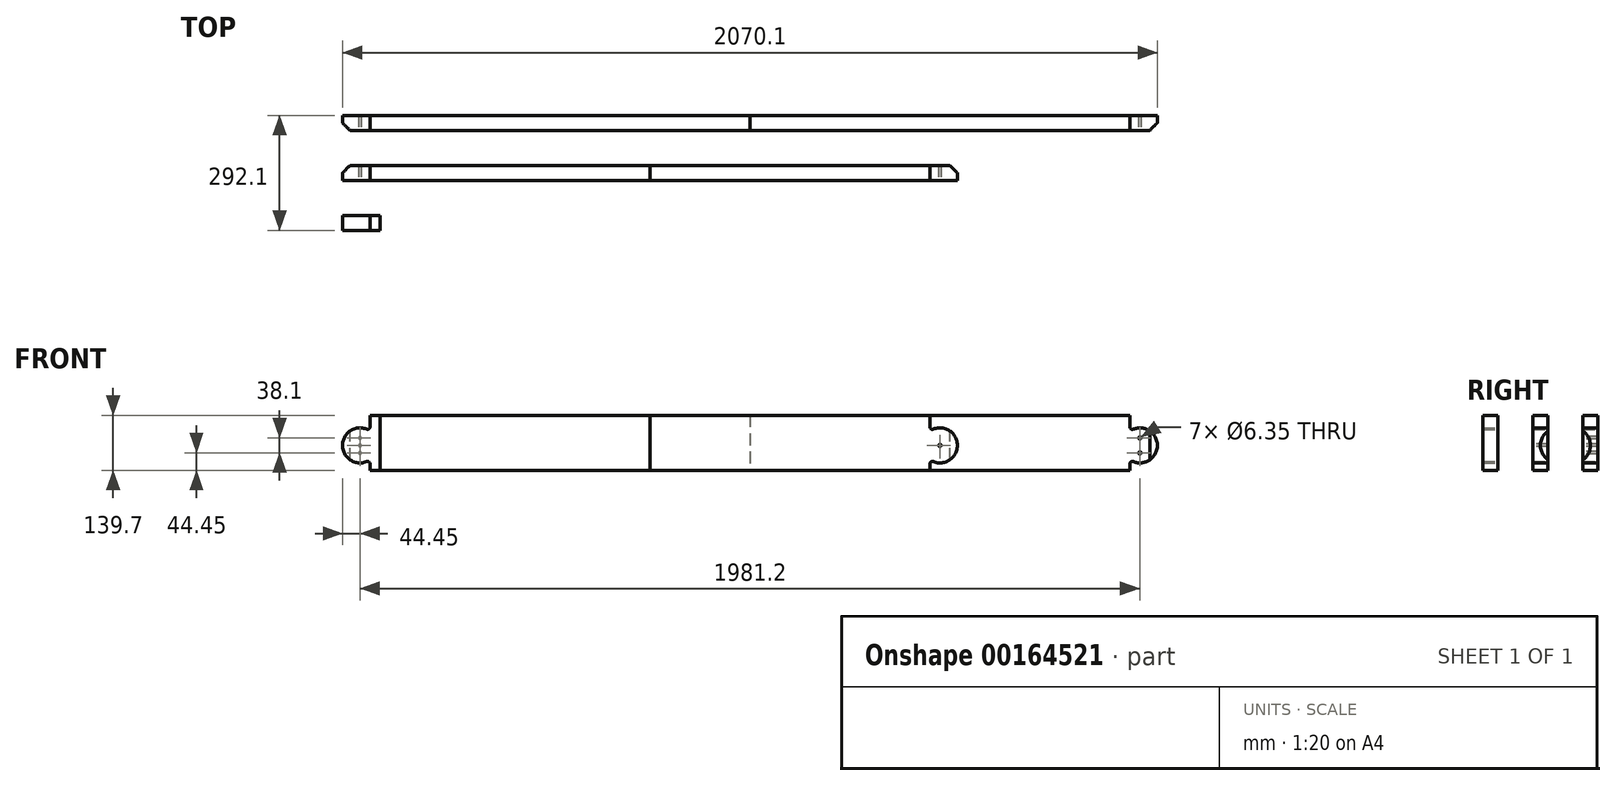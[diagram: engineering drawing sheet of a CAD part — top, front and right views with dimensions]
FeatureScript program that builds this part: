
annotation { "Feature Type Name" : "Feature", "Feature Type Description" : "" }
export const myFeature = defineFeature(function(context is Context, id is Id, definition is map)
    precondition{}
    {
        {
            var Q0;
            Q0=qCreatedBy(makeId("Front.planeOp"),FACE);
            var sketch = newSketch(context, id + "F0", { "sketchPlane" : qUnion([Q0])});
            skArc(sketch, "E0", {"start": v(25.4, 36.48) * mm, "mid": v(-44.45, 0) * mm, "end": v(25.4, -36.48) * mm});
            skLineSegment(sketch, "E1.bottom", {"start": v(50.8, 76.2) * mm, "end": v(25.4, 76.2) * mm});
            skLineSegment(sketch, "E1.top", {"start": v(50.8, -63.5) * mm, "end": v(25.4, -63.5) * mm});
            skLineSegment(sketch, "E1.left", {"start": v(50.8, 76.2) * mm, "end": v(50.8, -63.5) * mm});
            skLineSegment(sketch, "E1.right", {"start": v(25.4, 76.2) * mm, "end": v(25.4, 36.48) * mm});
            skPoint(sketch, "E1.middle", {"position": v(38.1, 6.35) * mm});
            skLineSegment(sketch, "E2.trimOffspring", {"start": v(25.4, -36.48) * mm, "end": v(25.4, -63.5) * mm});
            skSolve(sketch);
        }
        {
            var Q0;
            Q0=makeQuery(id+"F0.imprint","IMPRINT",FACE,{"disambiguationData":[TD([[makeQuery(id+"F0.imprint","IMPRINT",EDGE,{"derivedFrom":sQuery(id+"F0.wireOp",EDGE,"E0")}),1.0]])]});
            extrude(context, id + "F1", {"entities" : qUnion([Q0]), "depth" : 38.1 * mm});
        }
        {
            var Q0;
            Q0=makeQuery(id+"F1.opExtrude","SWEPT_EDGE",EDGE,{"disambiguationData":[OSD([sQuery(id+"F0.wireOp",EDGE,"E0"),sQuery(id+"F0.wireOp",EDGE,"E1.right")])]});
            var Q1;
            Q1=makeQuery(id+"F1.opExtrude","SWEPT_EDGE",EDGE,{"disambiguationData":[OSD([sQuery(id+"F0.wireOp",EDGE,"E0"),sQuery(id+"F0.wireOp",EDGE,"E2.trimOffspring")])]});
            fillet(context, id + "F2", {"entities" : qUnion([Q0, Q1]), "radius" : 6.35 * mm, "tangentPropagation" : true, "allowEdgeOverflow" : false});
        }
        {
            var Q0;
            Q0=makeQuery(id+"F1.opExtrude","SWEPT_BODY",BODY,{"disambiguationData":[OSD([sQuery(id+"F0.wireOp",EDGE,"E0"),sQuery(id+"F0.wireOp",EDGE,"E1.bottom"),sQuery(id+"F0.wireOp",EDGE,"E1.top"),sQuery(id+"F0.wireOp",EDGE,"E1.left"),sQuery(id+"F0.wireOp",EDGE,"E1.right"),sQuery(id+"F0.wireOp",EDGE,"E2.trimOffspring")])]});
            transform(context, id + "F3", {"entities" : qUnion([Q0]), "transformType" : TransformType.TRANSLATION_3D, "dx" : 0 * mm, "dy" : 254 * mm, "dz" : 0 * mm, "makeCopy" : true});
        }
        {
            var Q0;
            Q0=makeQuery(id+"F3.opPattern","COPY",FACE,{"derivedFrom":makeQuery(id+"F1.opExtrude","SWEPT_FACE",FACE,{"disambiguationData":[OSD([sQuery(id+"F0.wireOp",EDGE,"E1.left")])]}),"instanceName":"1"});
            extrude(context, id + "F4", {"entities" : qUnion([Q0]), "operationType" : NewBodyOperationType.ADD, "depth" : 939.8 * mm});
        }
        {
            var Q0;
            {var subQ0=sQuery(id+"F0.wireOp",EDGE,"E1.left");var subQ1=makeQuery(id+"F4.boolean.opBoolean","MERGE",FACE,{"derivedFrom":[makeQuery(id+"F3.opPattern","COPY",FACE,{"derivedFrom":makeQuery(id+"F1.opExtrude","CAP_FACE",FACE,{"disambiguationData":[OSD([sQuery(id+"F0.wireOp",EDGE,"E0"),sQuery(id+"F0.wireOp",EDGE,"E1.bottom"),sQuery(id+"F0.wireOp",EDGE,"E1.top"),subQ0,sQuery(id+"F0.wireOp",EDGE,"E1.right"),sQuery(id+"F0.wireOp",EDGE,"E2.trimOffspring")])],"isStart":false}),"instanceName":"1"}),makeQuery(id+"F4.opExtrude","SWEPT_FACE",FACE,{"disambiguationData":[OSD([subQ0]),TDD([makeQuery(id+"F3.opPattern","COPY",EDGE,{"derivedFrom":makeQuery(id+"F1.opExtrude","CAP_EDGE",EDGE,{"disambiguationData":[OSD([subQ0])],"isStart":false}),"instanceName":"1"})])]})]});Q0=makeQuery(id+"F9.boolean.opBoolean","MERGE",FACE,{"derivedFrom":[subQ1,makeQuery(id+"F9.opPattern","COPY",FACE,{"derivedFrom":subQ1,"instanceName":"1"})]});}
            var sketch = newSketch(context, id + "F5", { "sketchPlane" : qUnion([Q0])});
            skCircle(sketch, "E3", {"center": v(0, 19.05) * mm, "radius": 3.18 * mm});
            skLineSegment(sketch, "E4", {"start": v(0, 0) * mm, "end": v(0, 13.8) * mm, "construction": true});
            skLineSegment(sketch, "E5", {"start": v(0, 0) * mm, "end": v(19.07, 0) * mm, "construction": true});
            skCircle(sketch, "E6.MirrorC", {"center": v(0, -19.05) * mm, "radius": 3.18 * mm});
            skSolve(sketch);
        }
        {
            var Q0;
            Q0 = qSketchRegion(id + "F5", true);
            extrude(context, id + "F6", {"entities" : qUnion([Q0]), "operationType" : NewBodyOperationType.REMOVE, "endBound" : BoundingType.THROUGH_ALL, "oppositeDirection" : true, "depth" : 25.4 * mm});
        }
        {
            var Q0;
            Q0=qCreatedBy(makeId("Top.planeOp"),FACE);
            var sketch = newSketch(context, id + "F7", { "sketchPlane" : qUnion([Q0])});
            skLineSegment(sketch, "E7", {"start": v(-63.5, 254) * mm, "end": v(-63.5, 209.79) * mm});
            skLineSegment(sketch, "E8", {"start": v(-63.5, 209.79) * mm, "end": v(-19.29, 209.79) * mm});
            skLineSegment(sketch, "E9", {"start": v(-19.29, 209.79) * mm, "end": v(-63.5, 254) * mm});
            skSolve(sketch);
        }
        {
            var Q0;
            Q0 = qSketchRegion(id + "F7", true);
            extrude(context, id + "F8", {"entities" : qUnion([Q0]), "operationType" : NewBodyOperationType.REMOVE, "endBound" : BoundingType.SYMMETRIC, "oppositeDirection" : true, "depth" : 127 * mm});
        }
        {
            var Q0;
            Q0=makeQuery(id+"F3.opPattern","COPY",BODY,{"derivedFrom":makeQuery(id+"F1.opExtrude","SWEPT_BODY",BODY,{"disambiguationData":[OSD([sQuery(id+"F0.wireOp",EDGE,"E0"),sQuery(id+"F0.wireOp",EDGE,"E1.bottom"),sQuery(id+"F0.wireOp",EDGE,"E1.top"),sQuery(id+"F0.wireOp",EDGE,"E1.left"),sQuery(id+"F0.wireOp",EDGE,"E1.right"),sQuery(id+"F0.wireOp",EDGE,"E2.trimOffspring")])]}),"instanceName":"1"});
            var Q1;
            Q1=makeQuery(id+"F4.opExtrude","CAP_FACE",FACE,{"disambiguationData":[OSD([sQuery(id+"F0.wireOp",EDGE,"E1.left")])],"isStart":false});
            mirror(context, id + "F9", {"operationType" : NewBodyOperationType.ADD, "entities" : qUnion([Q0]), "mirrorPlane" : qUnion([Q1])});
        }
        {
            var Q0;
            Q0=makeQuery(id+"F1.opExtrude","SWEPT_BODY",BODY,{"disambiguationData":[OSD([sQuery(id+"F0.wireOp",EDGE,"E0"),sQuery(id+"F0.wireOp",EDGE,"E1.bottom"),sQuery(id+"F0.wireOp",EDGE,"E1.top"),sQuery(id+"F0.wireOp",EDGE,"E1.left"),sQuery(id+"F0.wireOp",EDGE,"E1.right"),sQuery(id+"F0.wireOp",EDGE,"E2.trimOffspring")])]});
            transform(context, id + "F10", {"entities" : qUnion([Q0]), "transformType" : TransformType.TRANSLATION_3D, "dx" : 0 * mm, "dy" : 127 * mm, "dz" : 0 * mm, "makeCopy" : true});
        }
        {
            var Q0;
            Q0=makeQuery(id+"F10.opPattern","COPY",FACE,{"derivedFrom":makeQuery(id+"F1.opExtrude","SWEPT_FACE",FACE,{"disambiguationData":[OSD([sQuery(id+"F0.wireOp",EDGE,"E1.left")])]}),"instanceName":"1"});
            extrude(context, id + "F11", {"entities" : qUnion([Q0]), "operationType" : NewBodyOperationType.ADD, "depth" : 685.8 * mm});
        }
        {
            var Q0;
            {var subQ0=sQuery(id+"F0.wireOp",EDGE,"E1.left");var subQ1=makeQuery(id+"F11.boolean.opBoolean","MERGE",FACE,{"derivedFrom":[makeQuery(id+"F10.opPattern","COPY",FACE,{"derivedFrom":makeQuery(id+"F1.opExtrude","CAP_FACE",FACE,{"disambiguationData":[OSD([sQuery(id+"F0.wireOp",EDGE,"E0"),sQuery(id+"F0.wireOp",EDGE,"E1.bottom"),sQuery(id+"F0.wireOp",EDGE,"E1.top"),subQ0,sQuery(id+"F0.wireOp",EDGE,"E1.right"),sQuery(id+"F0.wireOp",EDGE,"E2.trimOffspring")])],"isStart":false}),"instanceName":"1"}),makeQuery(id+"F11.opExtrude","SWEPT_FACE",FACE,{"disambiguationData":[OSD([subQ0]),TDD([makeQuery(id+"F10.opPattern","COPY",EDGE,{"derivedFrom":makeQuery(id+"F1.opExtrude","CAP_EDGE",EDGE,{"disambiguationData":[OSD([subQ0])],"isStart":false}),"instanceName":"1"})])]})]});Q0=makeQuery(id+"F16.boolean.opBoolean","MERGE",FACE,{"derivedFrom":[subQ1,makeQuery(id+"F16.opPattern","COPY",FACE,{"derivedFrom":subQ1,"instanceName":"1"})]});}
            var sketch = newSketch(context, id + "F12", { "sketchPlane" : qUnion([Q0])});
            skCircle(sketch, "E10", {"center": v(0, 0) * mm, "radius": 3.18 * mm});
            skSolve(sketch);
        }
        {
            var Q0;
            Q0 = qSketchRegion(id + "F12", true);
            extrude(context, id + "F13", {"entities" : qUnion([Q0]), "operationType" : NewBodyOperationType.REMOVE, "endBound" : BoundingType.THROUGH_ALL, "oppositeDirection" : true, "depth" : 25.4 * mm});
        }
        {
            var Q0;
            Q0=qCreatedBy(makeId("Top.planeOp"),FACE);
            var sketch = newSketch(context, id + "F14", { "sketchPlane" : qUnion([Q0])});
            skLineSegment(sketch, "E11", {"start": v(-63.5, 88.9) * mm, "end": v(-63.5, 152.4) * mm});
            skLineSegment(sketch, "E12", {"start": v(-63.5, 152.4) * mm, "end": v(0, 152.4) * mm});
            skLineSegment(sketch, "E13", {"start": v(0, 152.4) * mm, "end": v(-63.5, 88.9) * mm});
            skSolve(sketch);
        }
        {
            var Q0;
            Q0 = qSketchRegion(id + "F14", true);
            extrude(context, id + "F15", {"entities" : qUnion([Q0]), "operationType" : NewBodyOperationType.REMOVE, "endBound" : BoundingType.SYMMETRIC, "depth" : 101.6 * mm});
        }
        {
            var Q0;
            Q0=makeQuery(id+"F10.opPattern","COPY",BODY,{"derivedFrom":makeQuery(id+"F1.opExtrude","SWEPT_BODY",BODY,{"disambiguationData":[OSD([sQuery(id+"F0.wireOp",EDGE,"E0"),sQuery(id+"F0.wireOp",EDGE,"E1.bottom"),sQuery(id+"F0.wireOp",EDGE,"E1.top"),sQuery(id+"F0.wireOp",EDGE,"E1.left"),sQuery(id+"F0.wireOp",EDGE,"E1.right"),sQuery(id+"F0.wireOp",EDGE,"E2.trimOffspring")])]}),"instanceName":"1"});
            var Q1;
            Q1=makeQuery(id+"F11.opExtrude","CAP_FACE",FACE,{"disambiguationData":[OSD([sQuery(id+"F0.wireOp",EDGE,"E1.left")])],"isStart":false});
            mirror(context, id + "F16", {"operationType" : NewBodyOperationType.ADD, "entities" : qUnion([Q0]), "mirrorPlane" : qUnion([Q1])});
        }
    });
